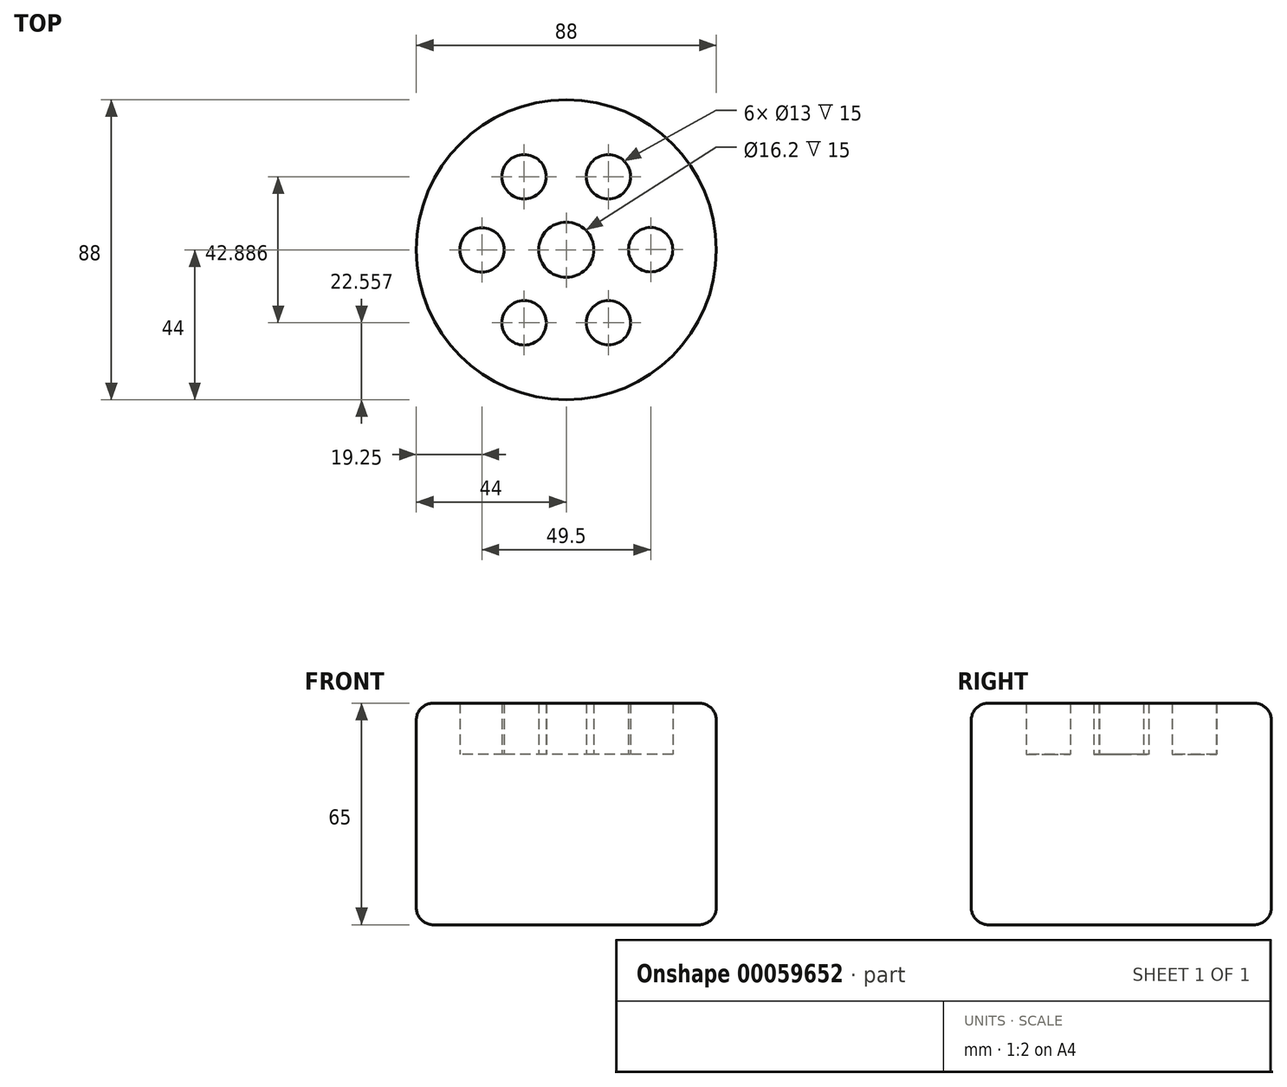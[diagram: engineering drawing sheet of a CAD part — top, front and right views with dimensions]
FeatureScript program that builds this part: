
annotation { "Feature Type Name" : "Feature", "Feature Type Description" : "" }
export const myFeature = defineFeature(function(context is Context, id is Id, definition is map)
    precondition{}
    {
        {
            var Q0;
            Q0=qCreatedBy(makeId("Top.planeOp"),FACE);
            var sketch = newSketch(context, id + "F0", { "sketchPlane" : qUnion([Q0])});
            skCircle(sketch, "E0.cCircle", {"center": v(0, 0) * mm, "radius": 21.43 * mm, "construction": true});
            skLineSegment(sketch, "E0.0", {"start": v(24.75, 0.02) * mm, "end": v(12.4, -21.43) * mm});
            skLineSegment(sketch, "E0.1", {"start": v(12.4, -21.43) * mm, "end": v(-12.36, -21.44) * mm});
            skLineSegment(sketch, "E0.2", {"start": v(-12.36, -21.44) * mm, "end": v(-24.75, -0.02) * mm});
            skLineSegment(sketch, "E0.3", {"start": v(-24.75, -0.02) * mm, "end": v(-12.4, 21.43) * mm});
            skLineSegment(sketch, "E0.4", {"start": v(-12.4, 21.43) * mm, "end": v(12.36, 21.44) * mm});
            skLineSegment(sketch, "E0.5", {"start": v(12.36, 21.44) * mm, "end": v(24.75, 0.02) * mm});
            skCircle(sketch, "E1", {"center": v(12.36, 21.44) * mm, "radius": 6.5 * mm});
            skCircle(sketch, "E2", {"center": v(-12.4, 21.43) * mm, "radius": 6.5 * mm});
            skCircle(sketch, "E3", {"center": v(-24.75, -0.02) * mm, "radius": 6.5 * mm});
            skCircle(sketch, "E4", {"center": v(-12.36, -21.44) * mm, "radius": 6.5 * mm});
            skCircle(sketch, "E5", {"center": v(12.4, -21.43) * mm, "radius": 6.5 * mm});
            skCircle(sketch, "E6", {"center": v(24.75, 0.02) * mm, "radius": 6.5 * mm});
            skCircle(sketch, "E7", {"center": v(0, 0) * mm, "radius": 44 * mm});
            skCircle(sketch, "E8", {"center": v(0, 0) * mm, "radius": 8.1 * mm});
            skSolve(sketch);
        }
        {
            var Q0;
            Q0=makeQuery(id+"F0.imprint","IMPRINT",FACE,{"disambiguationData":[TD([[makeQuery(id+"F0.imprint","IMPRINT",EDGE,{"derivedFrom":sQuery(id+"F0.wireOp",EDGE,"E7")}),1.0]])]});
            var Q1;
            Q1=makeQuery(id+"F0.imprint","IMPRINT",FACE,{"disambiguationData":[TD([[makeQuery(id+"F0.imprint","IMPRINT",EDGE,{"derivedFrom":sQuery(id+"F0.wireOp",EDGE,"E8")}),-1.0]])]});
            extrude(context, id + "F1", {"entities" : qUnion([Q0, Q1]), "depth" : 15 * mm});
        }
        {
            var Q0;
            {var subQ0=sQuery(id+"F0.wireOp",EDGE,"E0.2");var subQ1=sQuery(id+"F0.wireOp",EDGE,"E0.1");var subQ2=makeQuery(id+"F0.imprint","INTERSECT",VERTEX,{"derivedFrom":[subQ1,subQ0]});Q0=makeQuery(id+"F0.imprint","IMPRINT",FACE,{"disambiguationData":[TD([[makeQuery(id+"F0.imprint","IMPRINT",EDGE,{"disambiguationData":[TD([[subQ2,1.0]])],"derivedFrom":subQ1}),1.0]])]});}
            var Q1;
            {var subQ0=sQuery(id+"F0.wireOp",EDGE,"E0.2");var subQ1=sQuery(id+"F0.wireOp",EDGE,"E0.1");var subQ2=makeQuery(id+"F0.imprint","INTERSECT",VERTEX,{"derivedFrom":[subQ1,subQ0]});Q1=makeQuery(id+"F0.imprint","IMPRINT",FACE,{"disambiguationData":[TD([[makeQuery(id+"F0.imprint","IMPRINT",EDGE,{"disambiguationData":[TD([[subQ2,1.0]])],"derivedFrom":subQ1}),-1.0]])]});}
            var Q2;
            Q2=makeQuery(id+"F0.imprint","IMPRINT",FACE,{"disambiguationData":[TD([[makeQuery(id+"F0.imprint","IMPRINT",EDGE,{"derivedFrom":sQuery(id+"F0.wireOp",EDGE,"E8")}),1.0]])]});
            var Q3;
            {var subQ0=sQuery(id+"F0.wireOp",EDGE,"E0.3");var subQ1=sQuery(id+"F0.wireOp",EDGE,"E0.2");var subQ2=makeQuery(id+"F0.imprint","INTERSECT",VERTEX,{"derivedFrom":[subQ1,subQ0]});Q3=makeQuery(id+"F0.imprint","IMPRINT",FACE,{"disambiguationData":[TD([[makeQuery(id+"F0.imprint","IMPRINT",EDGE,{"disambiguationData":[TD([[subQ2,1.0]])],"derivedFrom":subQ1}),-1.0]])]});}
            var Q4;
            {var subQ0=sQuery(id+"F0.wireOp",EDGE,"E0.3");var subQ1=sQuery(id+"F0.wireOp",EDGE,"E0.2");var subQ2=makeQuery(id+"F0.imprint","INTERSECT",VERTEX,{"derivedFrom":[subQ1,subQ0]});Q4=makeQuery(id+"F0.imprint","IMPRINT",FACE,{"disambiguationData":[TD([[makeQuery(id+"F0.imprint","IMPRINT",EDGE,{"disambiguationData":[TD([[subQ2,1.0]])],"derivedFrom":subQ1}),1.0]])]});}
            var Q5;
            {var subQ0=sQuery(id+"F0.wireOp",EDGE,"E0.1");var subQ1=sQuery(id+"F0.wireOp",EDGE,"E0.0");var subQ2=makeQuery(id+"F0.imprint","INTERSECT",VERTEX,{"derivedFrom":[subQ1,subQ0]});Q5=makeQuery(id+"F0.imprint","IMPRINT",FACE,{"disambiguationData":[TD([[makeQuery(id+"F0.imprint","IMPRINT",EDGE,{"disambiguationData":[TD([[subQ2,1.0]])],"derivedFrom":subQ1}),1.0]])]});}
            var Q6;
            {var subQ0=sQuery(id+"F0.wireOp",EDGE,"E0.1");var subQ1=sQuery(id+"F0.wireOp",EDGE,"E0.0");var subQ2=makeQuery(id+"F0.imprint","INTERSECT",VERTEX,{"derivedFrom":[subQ1,subQ0]});Q6=makeQuery(id+"F0.imprint","IMPRINT",FACE,{"disambiguationData":[TD([[makeQuery(id+"F0.imprint","IMPRINT",EDGE,{"disambiguationData":[TD([[subQ2,1.0]])],"derivedFrom":subQ1}),-1.0]])]});}
            var Q7;
            {var subQ0=sQuery(id+"F0.wireOp",EDGE,"E0.5");var subQ1=sQuery(id+"F0.wireOp",EDGE,"E0.0");var subQ2=makeQuery(id+"F0.imprint","INTERSECT",VERTEX,{"derivedFrom":[subQ1,subQ0]});Q7=makeQuery(id+"F0.imprint","IMPRINT",FACE,{"disambiguationData":[TD([[makeQuery(id+"F0.imprint","IMPRINT",EDGE,{"disambiguationData":[TD([[subQ2,-1.0]])],"derivedFrom":subQ1}),1.0]])]});}
            var Q8;
            {var subQ0=sQuery(id+"F0.wireOp",EDGE,"E0.5");var subQ1=sQuery(id+"F0.wireOp",EDGE,"E0.0");var subQ2=makeQuery(id+"F0.imprint","INTERSECT",VERTEX,{"derivedFrom":[subQ1,subQ0]});Q8=makeQuery(id+"F0.imprint","IMPRINT",FACE,{"disambiguationData":[TD([[makeQuery(id+"F0.imprint","IMPRINT",EDGE,{"disambiguationData":[TD([[subQ2,-1.0]])],"derivedFrom":subQ1}),-1.0]])]});}
            var Q9;
            {var subQ0=sQuery(id+"F0.wireOp",EDGE,"E0.5");var subQ1=sQuery(id+"F0.wireOp",EDGE,"E0.4");var subQ2=makeQuery(id+"F0.imprint","INTERSECT",VERTEX,{"derivedFrom":[subQ1,subQ0]});Q9=makeQuery(id+"F0.imprint","IMPRINT",FACE,{"disambiguationData":[TD([[makeQuery(id+"F0.imprint","IMPRINT",EDGE,{"disambiguationData":[TD([[subQ2,1.0]])],"derivedFrom":subQ1}),1.0]])]});}
            var Q10;
            {var subQ0=sQuery(id+"F0.wireOp",EDGE,"E0.4");var subQ1=sQuery(id+"F0.wireOp",EDGE,"E0.3");var subQ2=makeQuery(id+"F0.imprint","INTERSECT",VERTEX,{"derivedFrom":[subQ1,subQ0]});Q10=makeQuery(id+"F0.imprint","IMPRINT",FACE,{"disambiguationData":[TD([[makeQuery(id+"F0.imprint","IMPRINT",EDGE,{"disambiguationData":[TD([[subQ2,1.0]])],"derivedFrom":subQ1}),1.0]])]});}
            var Q11;
            {var subQ0=sQuery(id+"F0.wireOp",EDGE,"E0.4");var subQ1=sQuery(id+"F0.wireOp",EDGE,"E0.3");var subQ2=makeQuery(id+"F0.imprint","INTERSECT",VERTEX,{"derivedFrom":[subQ1,subQ0]});Q11=makeQuery(id+"F0.imprint","IMPRINT",FACE,{"disambiguationData":[TD([[makeQuery(id+"F0.imprint","IMPRINT",EDGE,{"disambiguationData":[TD([[subQ2,1.0]])],"derivedFrom":subQ1}),-1.0]])]});}
            var Q12;
            {var subQ0=sQuery(id+"F0.wireOp",EDGE,"E0.5");var subQ1=sQuery(id+"F0.wireOp",EDGE,"E0.4");var subQ2=makeQuery(id+"F0.imprint","INTERSECT",VERTEX,{"derivedFrom":[subQ1,subQ0]});Q12=makeQuery(id+"F0.imprint","IMPRINT",FACE,{"disambiguationData":[TD([[makeQuery(id+"F0.imprint","IMPRINT",EDGE,{"disambiguationData":[TD([[subQ2,1.0]])],"derivedFrom":subQ1}),-1.0]])]});}
            var Q13;
            Q13=makeQuery(id+"F0.imprint","IMPRINT",FACE,{"disambiguationData":[TD([[makeQuery(id+"F0.imprint","IMPRINT",EDGE,{"derivedFrom":sQuery(id+"F0.wireOp",EDGE,"E8")}),-1.0]])]});
            var Q14;
            Q14=makeQuery(id+"F0.imprint","IMPRINT",FACE,{"disambiguationData":[TD([[makeQuery(id+"F0.imprint","IMPRINT",EDGE,{"derivedFrom":sQuery(id+"F0.wireOp",EDGE,"E7")}),1.0]])]});
            extrude(context, id + "F2", {"entities" : qUnion([Q0, Q1, Q2, Q3, Q4, Q5, Q6, Q7, Q8, Q9, Q10, Q11, Q12, Q13, Q14]), "operationType" : NewBodyOperationType.ADD, "oppositeDirection" : true, "depth" : 50 * mm});
        }
        {
            var Q0;
            Q0=makeQuery(id+"F1.opExtrude","CAP_EDGE",EDGE,{"disambiguationData":[OSD([sQuery(id+"F0.wireOp",EDGE,"E7")])],"isStart":false});
            var Q1;
            Q1=makeQuery(id+"F2.opExtrude","CAP_EDGE",EDGE,{"disambiguationData":[OSD([sQuery(id+"F0.wireOp",EDGE,"E7")])],"isStart":false});
            fillet(context, id + "F3", {"entities" : qUnion([Q0, Q1]), "radius" : 5 * mm, "tangentPropagation" : true, "allowEdgeOverflow" : false});
        }
    });
